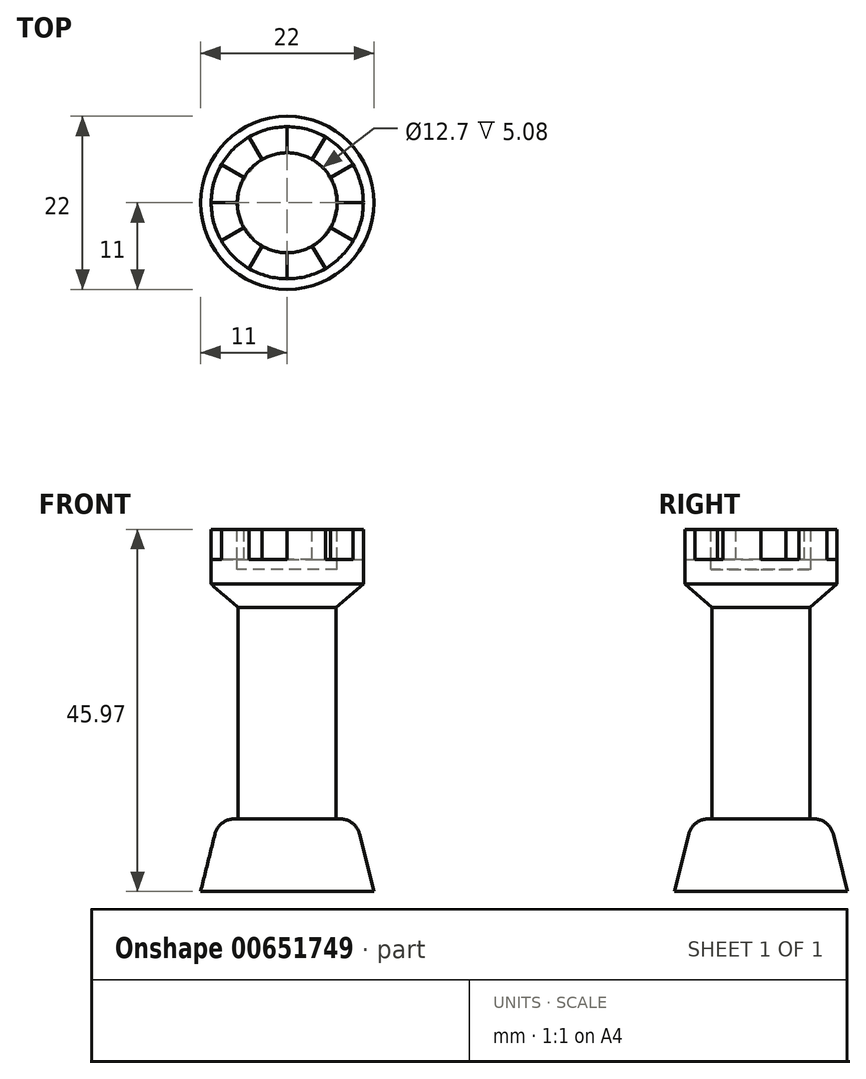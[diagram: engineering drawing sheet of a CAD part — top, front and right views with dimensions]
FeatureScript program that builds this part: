
annotation { "Feature Type Name" : "Feature", "Feature Type Description" : "" }
export const myFeature = defineFeature(function(context is Context, id is Id, definition is map)
    precondition{}
    {
        {
            var Q0;
            Q0=qCreatedBy(makeId("Front.planeOp"),FACE);
            var sketch = newSketch(context, id + "F0", { "sketchPlane" : qUnion([Q0])});
            skLineSegment(sketch, "E0", {"start": v(0, 45.97) * mm, "end": v(-9.66, 45.97) * mm});
            skLineSegment(sketch, "E1", {"start": v(-9.66, 45.97) * mm, "end": v(-9.66, 39.02) * mm});
            skLineSegment(sketch, "E2", {"start": v(-9.66, 39.02) * mm, "end": v(-6.22, 36.05) * mm});
            skLineSegment(sketch, "E3", {"start": v(0, 0) * mm, "end": v(-11, 0) * mm});
            skLineSegment(sketch, "E4", {"start": v(-11, 0) * mm, "end": v(-8.7, 9.2) * mm});
            skLineSegment(sketch, "E5", {"start": v(-8.7, 9.2) * mm, "end": v(-6.22, 9.2) * mm});
            skLineSegment(sketch, "E6", {"start": v(-6.22, 9.2) * mm, "end": v(-6.22, 36.05) * mm});
            skLineSegment(sketch, "E7", {"start": v(0, 0) * mm, "end": v(0, 45.97) * mm});
            skSolve(sketch);
        }
        {
            var Q0;
            Q0=makeQuery(id+"F0.imprint","IMPRINT",FACE,{"disambiguationData":[TD([[makeQuery(id+"F0.imprint","IMPRINT",EDGE,{"derivedFrom":sQuery(id+"F0.wireOp",EDGE,"E0")}),1.0]])]});
            var Q1;
            Q1=sQuery(id+"F0.wireOp",EDGE,"E7");
            revolve(context, id + "F1", {"entities" : qUnion([Q0]), "axis" : qUnion([Q1]), "revolveType" : RevolveType.FULL});
        }
        {
            var Q0;
            Q0=makeQuery(id+"F1.opRevolve","SWEPT_EDGE",EDGE,{"disambiguationData":[OSD([sQuery(id+"F0.wireOp",EDGE,"E4"),sQuery(id+"F0.wireOp",EDGE,"E5")])]});
            fillet(context, id + "F2", {"entities" : qUnion([Q0]), "radius" : 2.54 * mm, "tangentPropagation" : true, "allowEdgeOverflow" : false});
        }
        {
            var Q0;
            Q0=makeQuery(id+"F1.opRevolve","SWEPT_FACE",FACE,{"disambiguationData":[OSD([sQuery(id+"F0.wireOp",EDGE,"E0")])]});
            var sketch = newSketch(context, id + "F3", { "sketchPlane" : qUnion([Q0])});
            skCircle(sketch, "E8", {"center": v(0, 0) * mm, "radius": 6.35 * mm});
            skLineSegment(sketch, "E9", {"start": v(0, 6.35) * mm, "end": v(0, 9.66) * mm});
            skLineSegment(sketch, "E10", {"start": v(-3.18, 5.5) * mm, "end": v(-4.83, 8.37) * mm});
            skArc(sketch, "E11", {"start": v(0, 9.66) * mm, "mid": v(-2.5, 9.33) * mm, "end": v(-4.83, 8.37) * mm});
            skLineSegment(sketch, "E12.1.0", {"start": v(-5.5, 3.18) * mm, "end": v(-8.37, 4.83) * mm});
            skArc(sketch, "E12.1.1", {"start": v(-8.37, 4.83) * mm, "mid": v(-9.33, 2.5) * mm, "end": v(-9.66, 0) * mm});
            skLineSegment(sketch, "E12.1.2", {"start": v(-6.35, 0) * mm, "end": v(-9.66, 0) * mm});
            skLineSegment(sketch, "E12.2.0", {"start": v(-5.5, -3.17) * mm, "end": v(-8.37, -4.83) * mm});
            skArc(sketch, "E12.2.1", {"start": v(-8.37, -4.83) * mm, "mid": v(-6.83, -6.83) * mm, "end": v(-4.83, -8.37) * mm});
            skLineSegment(sketch, "E12.2.2", {"start": v(-3.17, -5.5) * mm, "end": v(-4.83, -8.37) * mm});
            skLineSegment(sketch, "E12.3.0", {"start": v(0, -6.35) * mm, "end": v(0, -9.66) * mm});
            skArc(sketch, "E12.3.1", {"start": v(0, -9.66) * mm, "mid": v(2.5, -9.33) * mm, "end": v(4.83, -8.37) * mm});
            skLineSegment(sketch, "E12.3.2", {"start": v(3.18, -5.5) * mm, "end": v(4.83, -8.37) * mm});
            skLineSegment(sketch, "E12.4.0", {"start": v(5.5, -3.18) * mm, "end": v(8.37, -4.83) * mm});
            skArc(sketch, "E12.4.1", {"start": v(8.37, -4.83) * mm, "mid": v(9.33, -2.5) * mm, "end": v(9.66, 0) * mm});
            skLineSegment(sketch, "E12.4.2", {"start": v(6.35, 0) * mm, "end": v(9.66, 0) * mm});
            skLineSegment(sketch, "E12.5.0", {"start": v(5.5, 3.18) * mm, "end": v(8.37, 4.83) * mm});
            skArc(sketch, "E12.5.1", {"start": v(8.37, 4.83) * mm, "mid": v(6.83, 6.83) * mm, "end": v(4.83, 8.37) * mm});
            skLineSegment(sketch, "E12.5.2", {"start": v(3.17, 5.5) * mm, "end": v(4.83, 8.37) * mm});
            skSolve(sketch);
        }
        {
            var Q0;
            {var subQ0=sQuery(id+"F3.wireOp",EDGE,"E10");Q0=makeQuery(id+"F3.imprint","IMPRINT",FACE,{"disambiguationData":[TD([[makeQuery(id+"F3.imprint","IMPRINT",EDGE,{"derivedFrom":subQ0}),1.0]])]});}
            var Q1;
            {var subQ0=sQuery(id+"F3.wireOp",EDGE,"E9");Q1=makeQuery(id+"F3.imprint","IMPRINT",FACE,{"disambiguationData":[TD([[makeQuery(id+"F3.imprint","IMPRINT",EDGE,{"derivedFrom":subQ0}),-1.0]])]});}
            var Q2;
            {var subQ0=sQuery(id+"F3.wireOp",EDGE,"E12.4.2");Q2=makeQuery(id+"F3.imprint","IMPRINT",FACE,{"disambiguationData":[TD([[makeQuery(id+"F3.imprint","IMPRINT",EDGE,{"derivedFrom":subQ0}),1.0]])]});}
            var Q3;
            {var subQ0=sQuery(id+"F3.wireOp",EDGE,"E12.3.2");Q3=makeQuery(id+"F3.imprint","IMPRINT",FACE,{"disambiguationData":[TD([[makeQuery(id+"F3.imprint","IMPRINT",EDGE,{"derivedFrom":subQ0}),1.0]])]});}
            var Q4;
            {var subQ0=sQuery(id+"F3.wireOp",EDGE,"E12.2.2");Q4=makeQuery(id+"F3.imprint","IMPRINT",FACE,{"disambiguationData":[TD([[makeQuery(id+"F3.imprint","IMPRINT",EDGE,{"derivedFrom":subQ0}),1.0]])]});}
            var Q5;
            {var subQ0=sQuery(id+"F3.wireOp",EDGE,"E12.1.2");Q5=makeQuery(id+"F3.imprint","IMPRINT",FACE,{"disambiguationData":[TD([[makeQuery(id+"F3.imprint","IMPRINT",EDGE,{"derivedFrom":subQ0}),1.0]])]});}
            extrude(context, id + "F4", {"entities" : qUnion([Q0, Q1, Q2, Q3, Q4, Q5]), "operationType" : NewBodyOperationType.REMOVE, "oppositeDirection" : true, "depth" : 3.8 * mm, "offsetDistance" : 25.4 * mm});
        }
        {
            var Q0;
            {var subQ0=sQuery(id+"F3.wireOp",EDGE,"E8");var subQ8=makeQuery(id+"F3.imprint","INTERSECT",VERTEX,{"derivedFrom":[sQuery(id+"F3.wireOp",EDGE,"E12.3.2"),subQ0]});Q0=makeQuery(id+"F3.imprint","IMPRINT",FACE,{"disambiguationData":[TD([[makeQuery(id+"F3.imprint","IMPRINT",EDGE,{"disambiguationData":[TD([[subQ8,-1.0]])],"derivedFrom":subQ0}),1.0]])]});}
            extrude(context, id + "F5", {"entities" : qUnion([Q0]), "operationType" : NewBodyOperationType.REMOVE, "oppositeDirection" : true, "depth" : 5.08 * mm, "offsetDistance" : 25.4 * mm});
        }
    });
